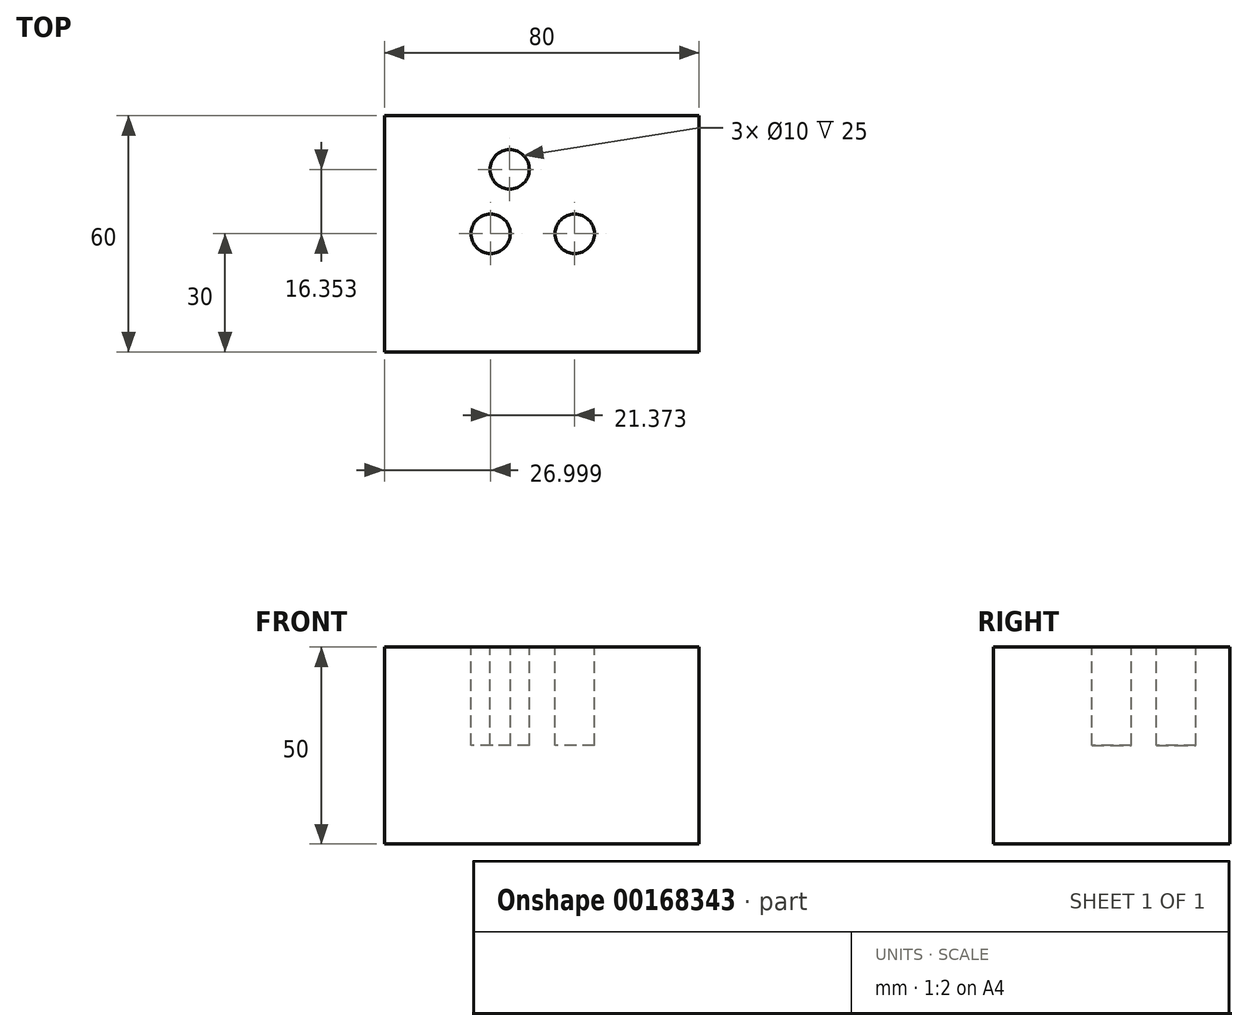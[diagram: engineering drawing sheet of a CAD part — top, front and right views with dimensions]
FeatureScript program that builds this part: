
annotation { "Feature Type Name" : "Feature", "Feature Type Description" : "" }
export const myFeature = defineFeature(function(context is Context, id is Id, definition is map)
    precondition{}
    {
        {
            var Q0;
            Q0=qCreatedBy(makeId("Top.planeOp"),FACE);
            var sketch = newSketch(context, id + "F0", { "sketchPlane" : qUnion([Q0])});
            skLineSegment(sketch, "E0.bottom", {"start": v(-40, 30) * mm, "end": v(40, 30) * mm});
            skLineSegment(sketch, "E0.top", {"start": v(-40, -30) * mm, "end": v(40, -30) * mm});
            skLineSegment(sketch, "E0.left", {"start": v(-40, 30) * mm, "end": v(-40, -30) * mm});
            skLineSegment(sketch, "E0.right", {"start": v(40, 30) * mm, "end": v(40, -30) * mm});
            skPoint(sketch, "E0.middle", {"position": v(0, 0) * mm});
            skSolve(sketch);
        }
        {
            var Q0;
            Q0 = qSketchRegion(id + "F0", true);
            extrude(context, id + "F1", {"entities" : qUnion([Q0]), "depth" : 50 * mm});
        }
        {
            var Q0;
            Q0=makeQuery(id+"F1.opExtrude","CAP_FACE",FACE,{"disambiguationData":[OSD([sQuery(id+"F0.wireOp",EDGE,"E0.bottom"),sQuery(id+"F0.wireOp",EDGE,"E0.top"),sQuery(id+"F0.wireOp",EDGE,"E0.left"),sQuery(id+"F0.wireOp",EDGE,"E0.right")])],"isStart":false});
            var sketch = newSketch(context, id + "F2", { "sketchPlane" : qUnion([Q0])});
            skCircle(sketch, "E1", {"center": v(-13, 0) * mm, "radius": 5 * mm});
            skCircle(sketch, "E2", {"center": v(8.37, 0) * mm, "radius": 5 * mm});
            skCircle(sketch, "E3", {"center": v(-8.15, 16.35) * mm, "radius": 5 * mm});
            skSolve(sketch);
        }
        {
            var Q0;
            Q0 = qSketchRegion(id + "F2", true);
            extrude(context, id + "F3", {"entities" : qUnion([Q0]), "operationType" : NewBodyOperationType.REMOVE, "oppositeDirection" : true, "depth" : 25 * mm});
        }
    });
